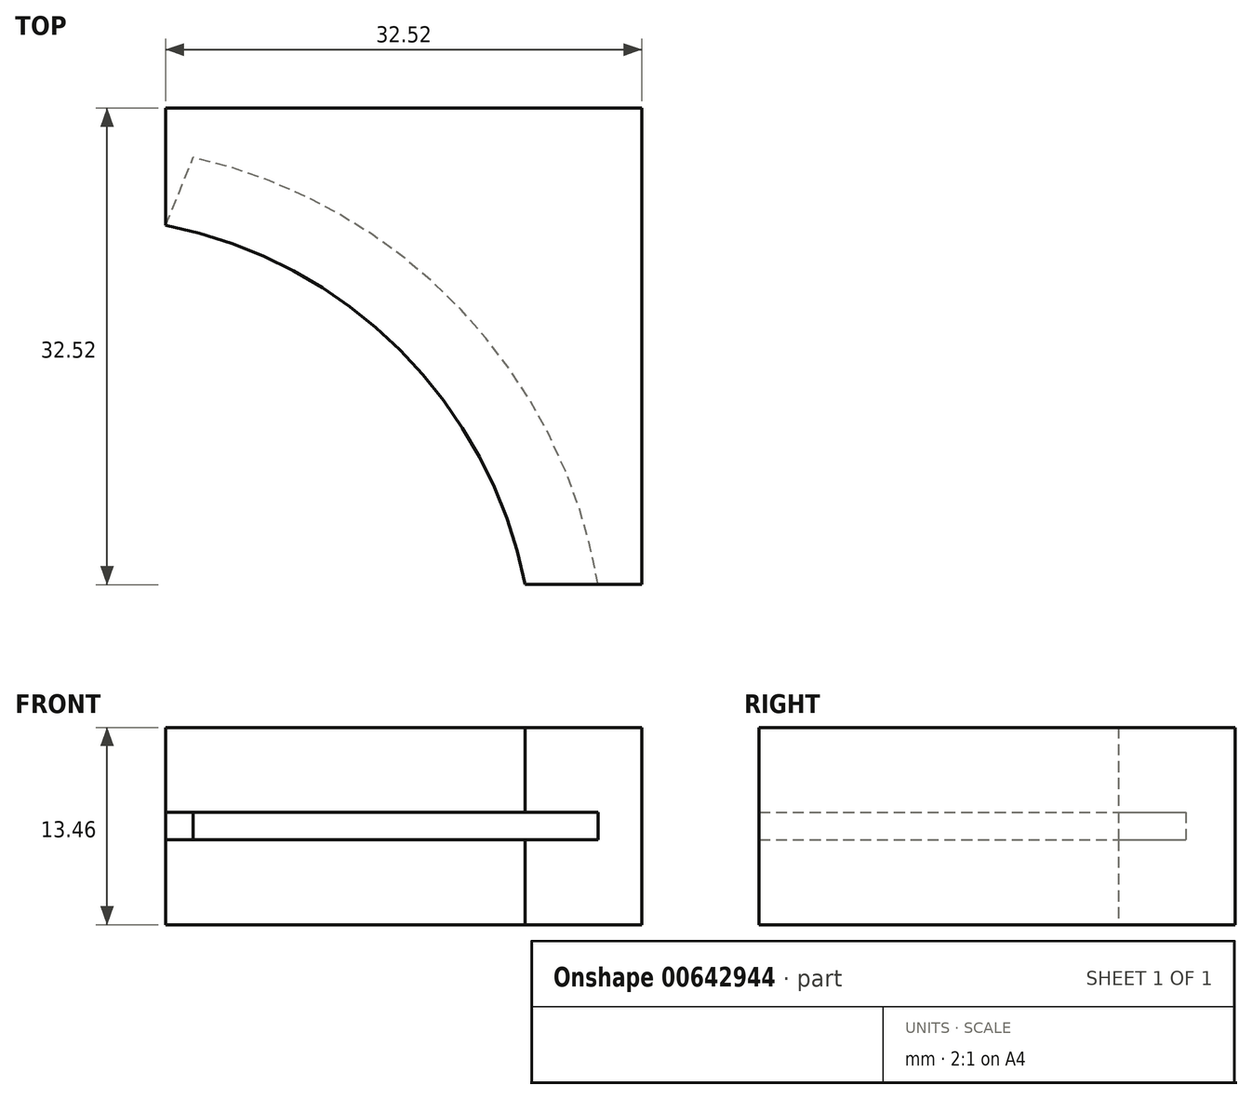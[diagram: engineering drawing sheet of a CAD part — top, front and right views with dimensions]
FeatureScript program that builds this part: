
annotation { "Feature Type Name" : "Feature", "Feature Type Description" : "" }
export const myFeature = defineFeature(function(context is Context, id is Id, definition is map)
    precondition{}
    {
        {
            var Q0;
            Q0=qCreatedBy(makeId("Top.planeOp"),FACE);
            var sketch = newSketch(context, id + "F0", { "sketchPlane" : qUnion([Q0])});
            skLineSegment(sketch, "E0", {"start": v(-32.52, 0) * mm, "end": v(0, 0) * mm});
            skLineSegment(sketch, "E1", {"start": v(0, 0) * mm, "end": v(0, -32.52) * mm});
            skLineSegment(sketch, "E2", {"start": v(0, 0) * mm, "end": v(-32.78, -32.78) * mm, "construction": true});
            skLineSegment(sketch, "E3", {"start": v(-32.52, 0) * mm, "end": v(-32.52, -7.98) * mm});
            skLineSegment(sketch, "E4", {"start": v(-7.98, -32.52) * mm, "end": v(0, -32.52) * mm});
            skArc(sketch, "E5", {"start": v(-7.98, -32.52) * mm, "mid": v(-16.51, -16.51) * mm, "end": v(-32.52, -7.98) * mm});
            skSolve(sketch);
        }
        {
            var Q0;
            Q0=makeQuery(id+"F0.imprint","IMPRINT",FACE,{"disambiguationData":[TD([[makeQuery(id+"F0.imprint","IMPRINT",EDGE,{"derivedFrom":sQuery(id+"F0.wireOp",EDGE,"E0")}),-1.0]])]});
            extrude(context, id + "F1", {"entities" : qUnion([Q0]), "depth" : 13.46 * mm, "offsetDistance" : 25.4 * mm});
        }
        {
            var Q0;
            Q0=makeQuery(id+"F1.opExtrude","SWEPT_FACE",FACE,{"disambiguationData":[OSD([sQuery(id+"F0.wireOp",EDGE,"E4")])]});
            var sketch = newSketch(context, id + "F2", { "sketchPlane" : qUnion([Q0])});
            skLineSegment(sketch, "E6.0", {"start": v(-7.98, 13.46) * mm, "end": v(-7.98, 0) * mm});
            skLineSegment(sketch, "E7", {"start": v(-7.98, 6.73) * mm, "end": v(0, 6.73) * mm, "construction": true});
            skLineSegment(sketch, "E8.bottom", {"start": v(-7.98, 7.68) * mm, "end": v(-3, 7.68) * mm});
            skLineSegment(sketch, "E8.top", {"start": v(-7.98, 5.79) * mm, "end": v(-3, 5.79) * mm});
            skLineSegment(sketch, "E8.left", {"start": v(-7.98, 7.68) * mm, "end": v(-7.98, 5.79) * mm});
            skLineSegment(sketch, "E8.right", {"start": v(-3, 7.68) * mm, "end": v(-3, 5.79) * mm});
            skSolve(sketch);
        }
        {
            var Q0;
            Q0=makeQuery(id+"F2.imprint","IMPRINT",FACE,{"disambiguationData":[TD([[makeQuery(id+"F2.imprint","IMPRINT",EDGE,{"derivedFrom":sQuery(id+"F2.wireOp",EDGE,"E8.bottom")}),-1.0]])]});
            var Q1;
            Q1=makeQuery(id+"F1.opExtrude","CAP_EDGE",EDGE,{"disambiguationData":[OSD([sQuery(id+"F0.wireOp",EDGE,"E5")])],"isStart":false});
            sweep(context, id + "F3", {"operationType" : NewBodyOperationType.REMOVE, "profiles" : qUnion([Q0]), "path" : qUnion([Q1])});
        }
    });
